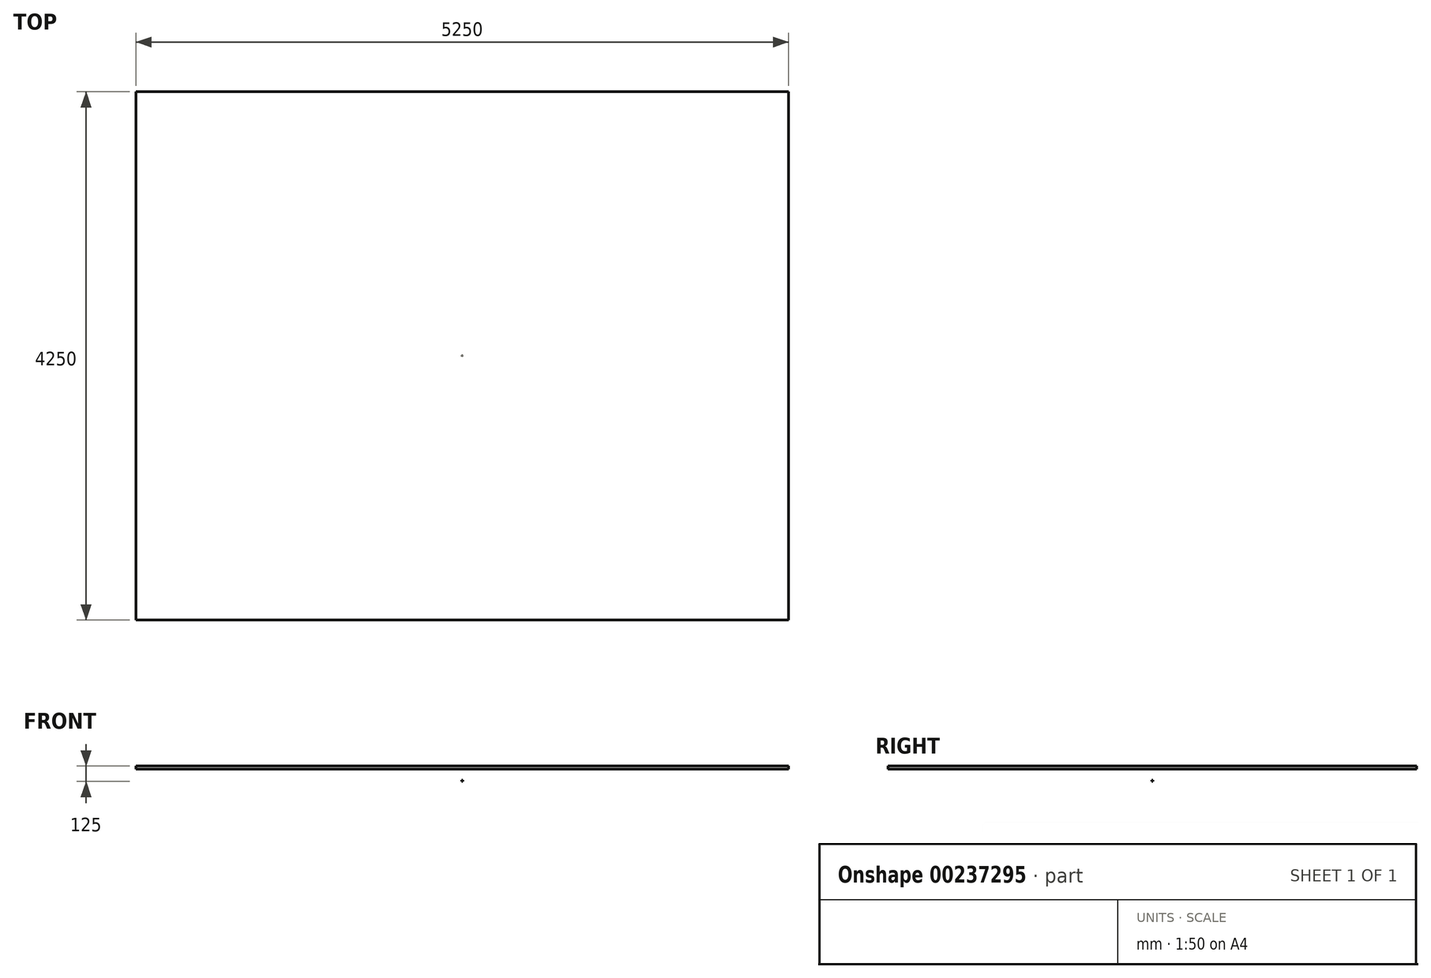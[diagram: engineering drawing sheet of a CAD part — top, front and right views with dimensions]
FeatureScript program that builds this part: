
annotation { "Feature Type Name" : "Feature", "Feature Type Description" : "" }
export const myFeature = defineFeature(function(context is Context, id is Id, definition is map)
    precondition{}
    {
        {
            var Q0;
            Q0=qCreatedBy(makeId("Top.planeOp"),FACE);
            var sketch = newSketch(context, id + "F0", { "sketchPlane" : qUnion([Q0])});
            skLineSegment(sketch, "E0.bottom", {"start": v(5, -5) * mm, "end": v(-5, -5) * mm});
            skLineSegment(sketch, "E0.top", {"start": v(5, 5) * mm, "end": v(-5, 5) * mm});
            skLineSegment(sketch, "E0.left", {"start": v(5, -5) * mm, "end": v(5, 5) * mm});
            skLineSegment(sketch, "E0.right", {"start": v(-5, -5) * mm, "end": v(-5, 5) * mm});
            skPoint(sketch, "E0.middle", {"position": v(0, 0) * mm});
            skSolve(sketch);
        }
        {
            var Q0;
            Q0=makeQuery(id+"F0.imprint","IMPRINT",FACE,{"disambiguationData":[TD([[makeQuery(id+"F0.imprint","IMPRINT",EDGE,{"derivedFrom":sQuery(id+"F0.wireOp",EDGE,"E0.bottom")}),-1.0]])]});
            extrude(context, id + "F1", {"entities" : qUnion([Q0]), "depth" : 10 * mm});
        }
        {
            var Q0;
            Q0=qCreatedBy(makeId("Top.planeOp"),FACE);
            cPlane(context, id + "F2", {"entities" : qUnion([Q0]), "cplaneType" : CPlaneType.OFFSET, "offset" : 100 * mm, "width" : 150 * mm, "height" : 150 * mm});
        }
        {
            var Q0;
            Q0=qCreatedBy(id+"F2.planeOp",FACE);
            var sketch = newSketch(context, id + "F3", { "sketchPlane" : qUnion([Q0])});
            skLineSegment(sketch, "E1.bottom", {"start": v(2625, -2125) * mm, "end": v(-2625, -2125) * mm});
            skLineSegment(sketch, "E1.top", {"start": v(2625, 2125) * mm, "end": v(-2625, 2125) * mm});
            skLineSegment(sketch, "E1.left", {"start": v(2625, -2125) * mm, "end": v(2625, 2125) * mm});
            skLineSegment(sketch, "E1.right", {"start": v(-2625, -2125) * mm, "end": v(-2625, 2125) * mm});
            skPoint(sketch, "E1.middle", {"position": v(0, 0) * mm});
            skSolve(sketch);
        }
        {
            var Q0;
            Q0=makeQuery(id+"F3.imprint","IMPRINT",FACE,{"disambiguationData":[TD([[makeQuery(id+"F3.imprint","IMPRINT",EDGE,{"derivedFrom":sQuery(id+"F3.wireOp",EDGE,"E1.bottom")}),-1.0]])]});
            extrude(context, id + "F4", {"entities" : qUnion([Q0]), "depth" : 25 * mm});
        }
    });
